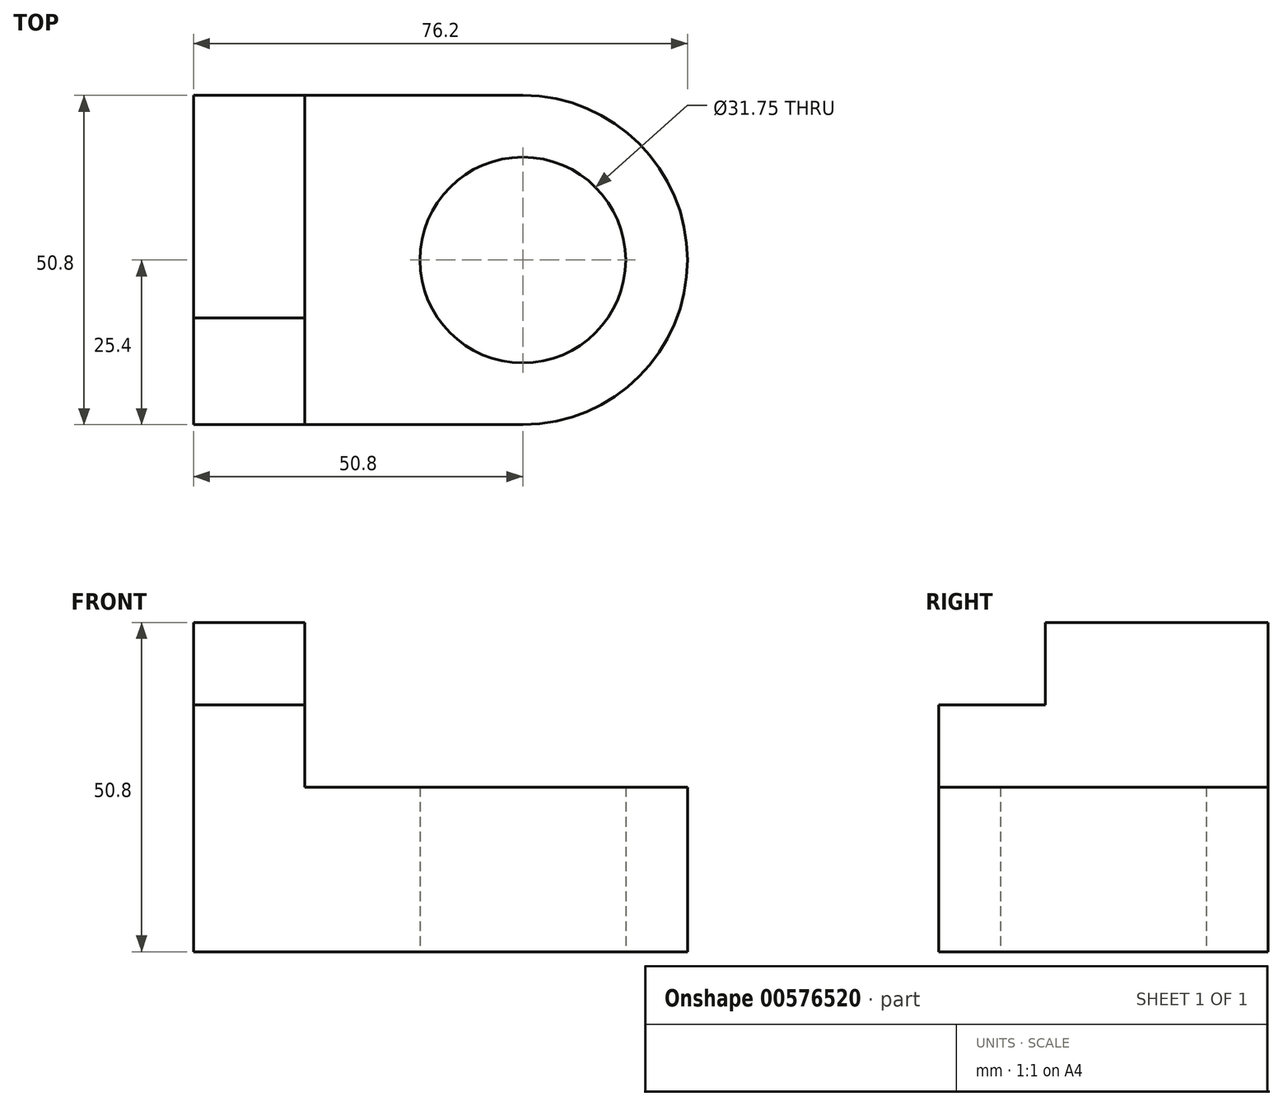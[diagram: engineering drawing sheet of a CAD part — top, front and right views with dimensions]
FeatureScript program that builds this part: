
annotation { "Feature Type Name" : "Feature", "Feature Type Description" : "" }
export const myFeature = defineFeature(function(context is Context, id is Id, definition is map)
    precondition{}
    {
        {
            var Q0;
            Q0=qCreatedBy(makeId("Top.planeOp"),FACE);
            var sketch = newSketch(context, id + "F0", { "sketchPlane" : qUnion([Q0])});
            skLineSegment(sketch, "E0.bottom", {"start": v(25.4, 25.4) * mm, "end": v(-25.4, 25.4) * mm});
            skLineSegment(sketch, "E0.top", {"start": v(25.4, -25.4) * mm, "end": v(-25.4, -25.4) * mm});
            skLineSegment(sketch, "E0.left", {"start": v(25.4, 25.4) * mm, "end": v(25.4, -25.4) * mm});
            skLineSegment(sketch, "E0.right", {"start": v(-25.4, 25.4) * mm, "end": v(-25.4, -25.4) * mm});
            skPoint(sketch, "E0.middle", {"position": v(0, 0) * mm});
            skSolve(sketch);
        }
        {
            var Q0;
            Q0=makeQuery(id+"F0.imprint","IMPRINT",FACE,{"disambiguationData":[TD([[makeQuery(id+"F0.imprint","IMPRINT",EDGE,{"derivedFrom":sQuery(id+"F0.wireOp",EDGE,"E0.bottom")}),1.0]])]});
            extrude(context, id + "F1", {"entities" : qUnion([Q0]), "depth" : 25.4 * mm, "offsetDistance" : 25.4 * mm});
        }
        {
            var Q0;
            Q0=makeQuery(id+"F1.opExtrude","SWEPT_FACE",FACE,{"disambiguationData":[OSD([sQuery(id+"F0.wireOp",EDGE,"E0.left")])]});
            var sketch = newSketch(context, id + "F2", { "sketchPlane" : qUnion([Q0])});
            skLineSegment(sketch, "E1.bottom", {"start": v(0, 0) * mm, "end": v(-25.4, 0) * mm});
            skLineSegment(sketch, "E1.top", {"start": v(0, 25.4) * mm, "end": v(-25.4, 25.4) * mm});
            skLineSegment(sketch, "E1.left", {"start": v(0, 0) * mm, "end": v(0, 25.4) * mm});
            skLineSegment(sketch, "E1.right", {"start": v(-25.4, 0) * mm, "end": v(-25.4, 25.4) * mm});
            skSolve(sketch);
        }
        {
            var Q0;
            Q0=makeQuery(id+"F2.imprint","IMPRINT",FACE,{"disambiguationData":[TD([[makeQuery(id+"F2.imprint","IMPRINT",EDGE,{"derivedFrom":sQuery(id+"F2.wireOp",EDGE,"E1.bottom")}),-1.0]])]});
            var Q1;
            Q1=sQuery(id+"F2.wireOp",EDGE,"E1.left");
            revolve(context, id + "F3", {"operationType" : NewBodyOperationType.ADD, "entities" : qUnion([Q0]), "axis" : qUnion([Q1]), "revolveType" : RevolveType.FULL});
        }
        {
            var Q0;
            Q0=makeQuery(id+"F3.boolean.opBoolean","MERGE",FACE,{"derivedFrom":[makeQuery(id+"F1.opExtrude","CAP_FACE",FACE,{"disambiguationData":[OSD([sQuery(id+"F0.wireOp",EDGE,"E0.bottom"),sQuery(id+"F0.wireOp",EDGE,"E0.top"),sQuery(id+"F0.wireOp",EDGE,"E0.left"),sQuery(id+"F0.wireOp",EDGE,"E0.right")])],"isStart":true}),makeQuery(id+"F3.opRevolve","SWEPT_FACE",FACE,{"disambiguationData":[OSD([sQuery(id+"F2.wireOp",EDGE,"E1.bottom")])]})]});
            var sketch = newSketch(context, id + "F4", { "sketchPlane" : qUnion([Q0])});
            skCircle(sketch, "E2", {"center": v(25.4, 0) * mm, "radius": 15.88 * mm});
            skSolve(sketch);
        }
        {
            var Q0;
            Q0=makeQuery(id+"F4.imprint","IMPRINT",FACE,{"disambiguationData":[TD([[makeQuery(id+"F4.imprint","IMPRINT",EDGE,{"derivedFrom":sQuery(id+"F4.wireOp",EDGE,"E2")}),1.0]])]});
            extrude(context, id + "F5", {"entities" : qUnion([Q0]), "operationType" : NewBodyOperationType.REMOVE, "endBound" : BoundingType.THROUGH_ALL, "oppositeDirection" : true, "depth" : 25.4 * mm, "offsetDistance" : 25.4 * mm});
        }
        {
            var Q0;
            Q0=makeQuery(id+"F3.boolean.opBoolean","MERGE",FACE,{"derivedFrom":[makeQuery(id+"F1.opExtrude","CAP_FACE",FACE,{"disambiguationData":[OSD([sQuery(id+"F0.wireOp",EDGE,"E0.bottom"),sQuery(id+"F0.wireOp",EDGE,"E0.top"),sQuery(id+"F0.wireOp",EDGE,"E0.left"),sQuery(id+"F0.wireOp",EDGE,"E0.right")])],"isStart":false}),makeQuery(id+"F3.opRevolve","SWEPT_FACE",FACE,{"disambiguationData":[OSD([sQuery(id+"F2.wireOp",EDGE,"E1.top")])]})]});
            var sketch = newSketch(context, id + "F6", { "sketchPlane" : qUnion([Q0])});
            skLineSegment(sketch, "E3.bottom", {"start": v(-25.4, -25.4) * mm, "end": v(-8.22, -25.4) * mm});
            skLineSegment(sketch, "E3.top", {"start": v(-25.4, 25.4) * mm, "end": v(-8.22, 25.4) * mm});
            skLineSegment(sketch, "E3.left", {"start": v(-25.4, -25.4) * mm, "end": v(-25.4, 25.4) * mm});
            skLineSegment(sketch, "E3.right", {"start": v(-8.22, -25.4) * mm, "end": v(-8.22, 25.4) * mm});
            skSolve(sketch);
        }
        {
            var Q0;
            Q0=makeQuery(id+"F6.imprint","IMPRINT",FACE,{"disambiguationData":[TD([[makeQuery(id+"F6.imprint","IMPRINT",EDGE,{"derivedFrom":sQuery(id+"F6.wireOp",EDGE,"E3.bottom")}),-1.0]])]});
            extrude(context, id + "F7", {"entities" : qUnion([Q0]), "operationType" : NewBodyOperationType.ADD, "depth" : 12.7 * mm, "offsetDistance" : 25.4 * mm});
        }
        {
            var Q0;
            Q0=makeQuery(id+"F7.opExtrude","CAP_FACE",FACE,{"disambiguationData":[OSD([sQuery(id+"F6.wireOp",EDGE,"E3.bottom"),sQuery(id+"F6.wireOp",EDGE,"E3.top"),sQuery(id+"F6.wireOp",EDGE,"E3.left"),sQuery(id+"F6.wireOp",EDGE,"E3.right")])],"isStart":false});
            var sketch = newSketch(context, id + "F8", { "sketchPlane" : qUnion([Q0])});
            skLineSegment(sketch, "E4.bottom", {"start": v(-25.4, 25.4) * mm, "end": v(-8.22, 25.4) * mm});
            skLineSegment(sketch, "E4.top", {"start": v(-25.4, -8.96) * mm, "end": v(-8.22, -8.96) * mm});
            skLineSegment(sketch, "E4.left", {"start": v(-25.4, 25.4) * mm, "end": v(-25.4, -8.96) * mm});
            skLineSegment(sketch, "E4.right", {"start": v(-8.22, 25.4) * mm, "end": v(-8.22, -8.96) * mm});
            skSolve(sketch);
        }
        {
            var Q0;
            Q0=makeQuery(id+"F8.imprint","IMPRINT",FACE,{"disambiguationData":[TD([[makeQuery(id+"F8.imprint","IMPRINT",EDGE,{"derivedFrom":sQuery(id+"F8.wireOp",EDGE,"E4.bottom")}),1.0]])]});
            extrude(context, id + "F9", {"entities" : qUnion([Q0]), "operationType" : NewBodyOperationType.ADD, "depth" : 12.7 * mm, "offsetDistance" : 25.4 * mm});
        }
    });
